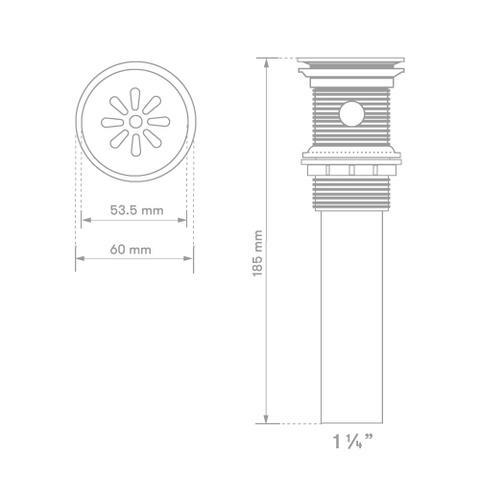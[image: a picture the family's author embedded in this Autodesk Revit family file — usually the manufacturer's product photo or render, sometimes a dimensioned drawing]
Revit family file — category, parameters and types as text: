
# Revit family: 01-3209-11 DESAGÜE PUSH CORTO CON REBOSE
name_source: partatom
category: Aparatos sanitarios
units: mm (PartAtom-declared; Revit-internal decimal feet)

## family parameters
Compartido = No
Corte con vacíos al cargar = No
Cota de conector redondo = Diámetro de uso
Número OmniClass = 23.45.00.00
Punto de cálculo de habitación = No
Se basa en plano de trabajo = No
Siempre vertical = Sí
Tipo de pieza = Normal
Título OmniClass = Sanitary, Laundry, and Cleaning Equipment

## types (1)
- 01-3209-11 DESAGÜE PUSH CORTO CON REBOSE
    Caucho = Caucho
    Conexión AC = No
    Conexión AF = No
    Conexión de residuos = No
    Conexión de ventilación = No
    Costo = 0 $
    Elevación por defecto = 0 mm  [stored 0 ft]
    Metal Laton Cromado = Metal Laton Cromado
    Nominal height = 130
    Nominal width = 370
    Plastico - ABS Cromado = Plastico - ABS Cromado
    Weight Net (Kg) = 6.60Kg

note: [stored X ft] marks values corroborated as IEEE doubles in the binary element streams (Revit-internal decimal feet)

## geometry (parser evidence)
native form markers: Blend x2, Sweep x1
no freeform markers — native parametric forms only
